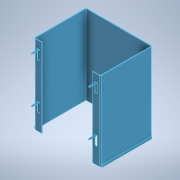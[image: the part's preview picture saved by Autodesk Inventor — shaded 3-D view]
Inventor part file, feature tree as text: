
AUTODESK INVENTOR PART (.ipt)
format: ipt  version: 2021 (Build 250183000, 183)  size: 292,864 bytes
history: native  units: mm
features: sheet_metal_op x16, sketch x9, other x6, chamfer x1, pattern_linear x1
ambient origin geometry x8: Origin, YZ Plane, XZ Plane, XY Plane, X Axis, Y Axis, Z Axis, Center Point
bodies: Solid1 (feature_tree)
feature tree (33):
  sheet_metal_op  "Face1"
  sheet_metal_op  "Flange1"
  sheet_metal_op  "Hem1"
  sheet_metal_op  "Hem2"
  sheet_metal_op  "Hem3"
  sheet_metal_op  "Flange2"
  sheet_metal_op  "Flange3"
  sheet_metal_op  "Flange4"
  chamfer  "Corner Round1"
  pattern_linear  "Rectangular Pattern1"  Spacing1=4.0mm  [1 undecoded]
  sketch  "Sketch1"  dims[d1=123.0mm]
  other  "Plate1"
  sketch  "Sketch2"  dims[d2=61.5mm]
  other  "Plate2"
  sheet_metal_op  "Bend1"
  sheet_metal_op  "Corner1"
  sketch  "Sketch6"  dims[d6=0.5mm]
  other  "Plate3"
  sheet_metal_op  "Bend2"
  sheet_metal_op  "Corner2"
  sketch  "Sketch7"  dims[d7=2.0mm]
  other  "Plate4"
  sheet_metal_op  "Bend3"
  sheet_metal_op  "Corner3"
  sketch  "Sketch9"  dims[d8=1.0mm]
  sketch  "Sketch10"  dims[d10=90.0deg d11=1.0mm d12=4.0mm d13=1.0mm d14=1.0mm d15=1.0mm d16=0.5mm d17=2.0mm d18=1.0mm d21=4.0mm d22=0.1mm d23=0.05mm d24=1.0mm d25=0.5mm d26=2.0mm d27=1.0mm d30=4.0mm d31=0.1mm d32=0.05mm d33=1.0mm d34=0.5mm d35=2.0mm d36=1.0mm d37=4.0mm d38=0.1mm d39=0.05mm d40=0.0mm d41=2.0mm d42=2.0mm d43=0.0mm d44=1.0mm d45=0.5mm d46=2.0mm d47=1.0mm d49=90.0deg d50=1.0mm d51=4.0mm d52=1.0mm d53=1.0mm d54=1.0mm d55=0.5mm d56=2.0mm d57=1.0mm d58=12.0mm d59=90.0deg d60=1.0mm d61=4.0mm d62=1.0mm d63=1.0mm d64=5.0mm d65=4.0mm d66=12.0mm d67=13.0mm d68=1.0mm d69=0.0mm d70=1.0mm d71=0.5mm d72=2.0mm d73=1.0mm d74=12.0mm d75=90.0deg d76=0.2mm d77=4.0mm d78=1.0mm d79=1.0mm d80=1.0mm d81=20.0mm d83=70.0mm d84=20.0mm d86=88.0mm]
  other  "Plate5"
  sheet_metal_op  "Bend4"
  sheet_metal_op  "Corner4"
  other  "Cut1"
  sketch  "Sketch3"  dims[d3=51.0mm]
  sketch  "Sketch4"  dims[d4=1.0mm]
  sketch  "Sketch5"  dims[d5=1.0mm]
note: 1 required parameter value undecoded (feature->parameter linkage not recoverable at this tier; creation-order binding heuristic only, values carry confidence <= 0.55)
